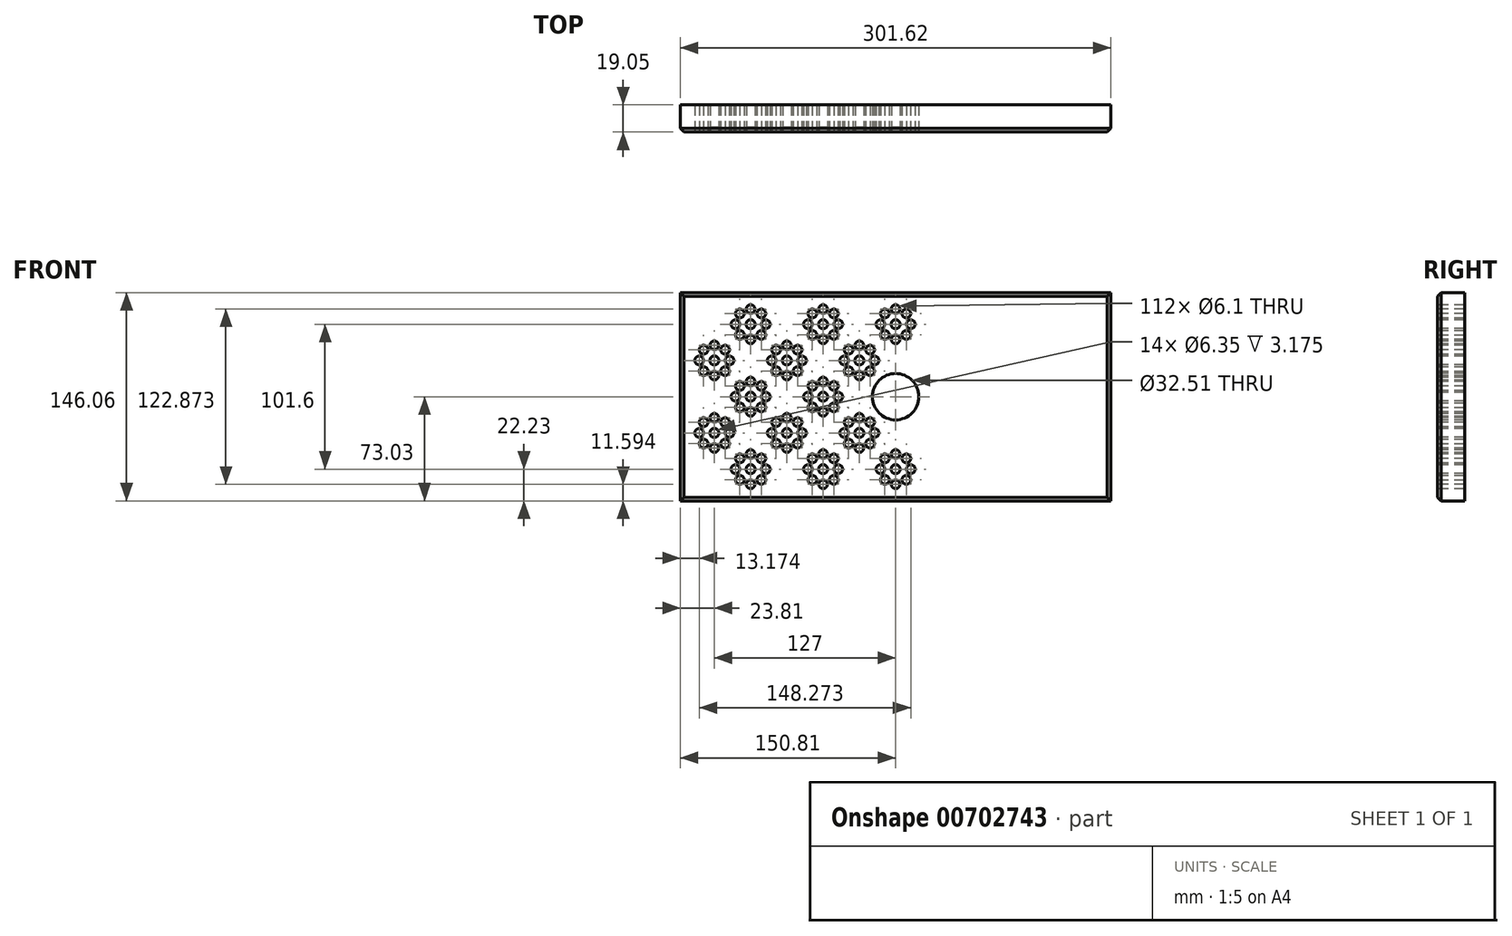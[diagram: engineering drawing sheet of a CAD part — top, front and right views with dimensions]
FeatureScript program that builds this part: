
annotation { "Feature Type Name" : "Feature", "Feature Type Description" : "" }
export const myFeature = defineFeature(function(context is Context, id is Id, definition is map)
    precondition{}
    {
        {
            var Q0;
            Q0=qCreatedBy(makeId("Front.planeOp"),FACE);
            var sketch = newSketch(context, id + "F0", { "sketchPlane" : qUnion([Q0])});
            skLineSegment(sketch, "E0.bottom", {"start": v(-150.81, 73.03) * mm, "end": v(150.81, 73.03) * mm});
            skLineSegment(sketch, "E0.top", {"start": v(-150.81, -73.03) * mm, "end": v(150.81, -73.03) * mm});
            skLineSegment(sketch, "E0.left", {"start": v(-150.81, 73.03) * mm, "end": v(-150.81, -73.03) * mm});
            skLineSegment(sketch, "E0.right", {"start": v(150.81, 73.03) * mm, "end": v(150.81, -73.03) * mm});
            skPoint(sketch, "E0.middle", {"position": v(0, 0) * mm});
            skSolve(sketch);
        }
        {
            var Q0;
            Q0 = qSketchRegion(id + "F0", true);
            extrude(context, id + "F1", {"entities" : qUnion([Q0]), "depth" : 19.05 * mm, "offsetDistance" : 25.4 * mm});
        }
        {
            var Q0;
            Q0=makeQuery(id+"F1.opExtrude","CAP_FACE",FACE,{"disambiguationData":[OSD([sQuery(id+"F0.wireOp",EDGE,"E0.bottom"),sQuery(id+"F0.wireOp",EDGE,"E0.top"),sQuery(id+"F0.wireOp",EDGE,"E0.left"),sQuery(id+"F0.wireOp",EDGE,"E0.right")])],"isStart":false});
            var sketch = newSketch(context, id + "F2", { "sketchPlane" : qUnion([Q0])});
            skLineSegment(sketch, "E1", {"start": v(-150.81, 25.4) * mm, "end": v(150.81, 25.4) * mm, "construction": true});
            skLineSegment(sketch, "E2", {"start": v(-150.81, 0) * mm, "end": v(150.81, 0) * mm, "construction": true});
            skLineSegment(sketch, "E3", {"start": v(-150.81, -25.4) * mm, "end": v(150.81, -25.4) * mm, "construction": true});
            skLineSegment(sketch, "E4", {"start": v(-101.6, 73.03) * mm, "end": v(-101.6, -73.03) * mm, "construction": true});
            skLineSegment(sketch, "E5", {"start": v(-50.8, 73.03) * mm, "end": v(-50.8, -73.03) * mm, "construction": true});
            skCircle(sketch, "E6", {"center": v(0, 0) * mm, "radius": 16.26 * mm});
            skLineSegment(sketch, "E7", {"start": v(-76.2, 73.03) * mm, "end": v(-76.2, -73.03) * mm, "construction": true});
            skLineSegment(sketch, "E8", {"start": v(-25.4, 73.03) * mm, "end": v(-25.4, -73.03) * mm, "construction": true});
            skLineSegment(sketch, "E9", {"start": v(-127, 73.03) * mm, "end": v(-127, -73.03) * mm, "construction": true});
            skCircle(sketch, "E10", {"center": v(-25.4, 25.4) * mm, "radius": 3.18 * mm});
            skCircle(sketch, "E11", {"center": v(-25.4, -25.4) * mm, "radius": 3.18 * mm});
            skCircle(sketch, "E12", {"center": v(-50.8, 0) * mm, "radius": 3.18 * mm});
            skCircle(sketch, "E13", {"center": v(-76.2, 25.4) * mm, "radius": 3.18 * mm});
            skCircle(sketch, "E14", {"center": v(-76.2, -25.4) * mm, "radius": 3.18 * mm});
            skCircle(sketch, "E15", {"center": v(-101.6, 0) * mm, "radius": 3.18 * mm});
            skCircle(sketch, "E16", {"center": v(-127, 25.4) * mm, "radius": 3.18 * mm});
            skCircle(sketch, "E17", {"center": v(-127, -25.4) * mm, "radius": 3.18 * mm});
            skLineSegment(sketch, "E18", {"start": v(-150.81, 50.8) * mm, "end": v(150.81, 50.8) * mm, "construction": true});
            skLineSegment(sketch, "E19", {"start": v(-150.81, -50.8) * mm, "end": v(150.81, -50.8) * mm, "construction": true});
            skCircle(sketch, "E20", {"center": v(-101.6, 50.8) * mm, "radius": 3.18 * mm});
            skCircle(sketch, "E21", {"center": v(-50.8, 50.8) * mm, "radius": 3.18 * mm});
            skCircle(sketch, "E22", {"center": v(0, 50.8) * mm, "radius": 3.18 * mm});
            skCircle(sketch, "E23", {"center": v(0, -50.8) * mm, "radius": 3.18 * mm});
            skCircle(sketch, "E24", {"center": v(-50.8, -50.8) * mm, "radius": 3.18 * mm});
            skCircle(sketch, "E25", {"center": v(-101.6, -50.8) * mm, "radius": 3.18 * mm});
            skSolve(sketch);
        }
        {
            var Q0;
            Q0 = qSketchRegion(id + "F2", true);
            extrude(context, id + "F3", {"entities" : qUnion([Q0]), "operationType" : NewBodyOperationType.REMOVE, "oppositeDirection" : true, "depth" : 3.17 * mm, "offsetDistance" : 25.4 * mm});
        }
        {
            var Q0;
            Q0=makeQuery(id+"F1.opExtrude","CAP_FACE",FACE,{"disambiguationData":[OSD([sQuery(id+"F0.wireOp",EDGE,"E0.bottom"),sQuery(id+"F0.wireOp",EDGE,"E0.top"),sQuery(id+"F0.wireOp",EDGE,"E0.left"),sQuery(id+"F0.wireOp",EDGE,"E0.right")])],"isStart":false});
            var sketch = newSketch(context, id + "F4", { "sketchPlane" : qUnion([Q0])});
            skCircle(sketch, "E26", {"center": v(-127, 25.4) * mm, "radius": 10.64 * mm, "construction": true});
            skCircle(sketch, "E27", {"center": v(-134.52, 32.92) * mm, "radius": 3.05 * mm});
            skCircle(sketch, "E28.1.0", {"center": v(-137.64, 25.4) * mm, "radius": 3.05 * mm});
            skCircle(sketch, "E28.2.0", {"center": v(-134.52, 17.88) * mm, "radius": 3.05 * mm});
            skCircle(sketch, "E29.1.3.0", {"center": v(-127, 14.76) * mm, "radius": 3.05 * mm});
            skCircle(sketch, "E29.1.4.0", {"center": v(-119.48, 17.88) * mm, "radius": 3.05 * mm});
            skCircle(sketch, "E29.1.5.0", {"center": v(-116.36, 25.4) * mm, "radius": 3.05 * mm});
            skCircle(sketch, "E29.1.6.0", {"center": v(-119.48, 32.92) * mm, "radius": 3.05 * mm});
            skCircle(sketch, "E29.1.7.0", {"center": v(-127, 36.04) * mm, "radius": 3.05 * mm});
            skLineSegment(sketch, "E30", {"start": v(-127, 25.4) * mm, "end": v(-127, 36.04) * mm, "construction": true});
            skSolve(sketch);
        }
        {
            var Q0;
            Q0=makeQuery(id+"F4.imprint","IMPRINT",FACE,{"disambiguationData":[TD([[makeQuery(id+"F4.imprint","IMPRINT",EDGE,{"derivedFrom":sQuery(id+"F4.wireOp",EDGE,"E27")}),1.0]])]});
            var Q1;
            Q1=makeQuery(id+"F4.imprint","IMPRINT",FACE,{"disambiguationData":[TD([[makeQuery(id+"F4.imprint","IMPRINT",EDGE,{"derivedFrom":sQuery(id+"F4.wireOp",EDGE,"E28.1.0")}),1.0]])]});
            var Q2;
            Q2=makeQuery(id+"F4.imprint","IMPRINT",FACE,{"disambiguationData":[TD([[makeQuery(id+"F4.imprint","IMPRINT",EDGE,{"derivedFrom":sQuery(id+"F4.wireOp",EDGE,"E28.2.0")}),1.0]])]});
            var Q3;
            Q3=makeQuery(id+"F4.imprint","IMPRINT",FACE,{"disambiguationData":[TD([[makeQuery(id+"F4.imprint","IMPRINT",EDGE,{"derivedFrom":sQuery(id+"F4.wireOp",EDGE,"E29.1.3.0")}),1.0]])]});
            var Q4;
            Q4=makeQuery(id+"F4.imprint","IMPRINT",FACE,{"disambiguationData":[TD([[makeQuery(id+"F4.imprint","IMPRINT",EDGE,{"derivedFrom":sQuery(id+"F4.wireOp",EDGE,"E29.1.4.0")}),1.0]])]});
            var Q5;
            Q5=makeQuery(id+"F4.imprint","IMPRINT",FACE,{"disambiguationData":[TD([[makeQuery(id+"F4.imprint","IMPRINT",EDGE,{"derivedFrom":sQuery(id+"F4.wireOp",EDGE,"E29.1.5.0")}),1.0]])]});
            var Q6;
            Q6=makeQuery(id+"F4.imprint","IMPRINT",FACE,{"disambiguationData":[TD([[makeQuery(id+"F4.imprint","IMPRINT",EDGE,{"derivedFrom":sQuery(id+"F4.wireOp",EDGE,"E29.1.6.0")}),1.0]])]});
            var Q7;
            Q7=makeQuery(id+"F4.imprint","IMPRINT",FACE,{"disambiguationData":[TD([[makeQuery(id+"F4.imprint","IMPRINT",EDGE,{"derivedFrom":sQuery(id+"F4.wireOp",EDGE,"E29.1.7.0")}),1.0]])]});
            extrude(context, id + "F5", {"entities" : qUnion([Q0, Q1, Q2, Q3, Q4, Q5, Q6, Q7]), "operationType" : NewBodyOperationType.REMOVE, "oppositeDirection" : true, "depth" : 25.4 * mm, "offsetDistance" : 25.4 * mm});
        }
        {
            var Q0;
            Q0=makeQuery(id+"F1.opExtrude","CAP_FACE",FACE,{"disambiguationData":[OSD([sQuery(id+"F0.wireOp",EDGE,"E0.bottom"),sQuery(id+"F0.wireOp",EDGE,"E0.top"),sQuery(id+"F0.wireOp",EDGE,"E0.left"),sQuery(id+"F0.wireOp",EDGE,"E0.right")])],"isStart":false});
            var sketch = newSketch(context, id + "F6", { "sketchPlane" : qUnion([Q0])});
            skCircle(sketch, "E31", {"center": v(0, 0) * mm, "radius": 16.26 * mm});
            skSolve(sketch);
        }
        {
            var Q0;
            Q0 = qSketchRegion(id + "F6", true);
            extrude(context, id + "F7", {"entities" : qUnion([Q0]), "operationType" : NewBodyOperationType.REMOVE, "oppositeDirection" : true, "depth" : 25.4 * mm, "offsetDistance" : 25.4 * mm});
        }
        {
            var Q0;
            Q0=makeQuery(id+"F1.opExtrude","CAP_FACE",FACE,{"disambiguationData":[OSD([sQuery(id+"F0.wireOp",EDGE,"E0.bottom"),sQuery(id+"F0.wireOp",EDGE,"E0.top"),sQuery(id+"F0.wireOp",EDGE,"E0.left"),sQuery(id+"F0.wireOp",EDGE,"E0.right")])],"isStart":false});
            var sketch = newSketch(context, id + "F8", { "sketchPlane" : qUnion([Q0])});
            skCircle(sketch, "E32", {"center": v(-76.2, 25.4) * mm, "radius": 10.64 * mm, "construction": true});
            skCircle(sketch, "E33", {"center": v(-83.72, 32.92) * mm, "radius": 3.05 * mm});
            skCircle(sketch, "E34.1.0", {"center": v(-86.84, 25.4) * mm, "radius": 3.05 * mm});
            skCircle(sketch, "E34.2.0", {"center": v(-83.72, 17.88) * mm, "radius": 3.05 * mm});
            skCircle(sketch, "E35.1.3.0", {"center": v(-76.2, 14.76) * mm, "radius": 3.05 * mm});
            skCircle(sketch, "E35.1.4.0", {"center": v(-68.68, 17.88) * mm, "radius": 3.05 * mm});
            skCircle(sketch, "E35.1.5.0", {"center": v(-65.56, 25.4) * mm, "radius": 3.05 * mm});
            skCircle(sketch, "E35.1.6.0", {"center": v(-68.68, 32.92) * mm, "radius": 3.05 * mm});
            skCircle(sketch, "E35.1.7.0", {"center": v(-76.2, 36.04) * mm, "radius": 3.05 * mm});
            skLineSegment(sketch, "E36", {"start": v(-76.2, 25.4) * mm, "end": v(-76.2, 36.04) * mm, "construction": true});
            skCircle(sketch, "E37", {"center": v(-25.4, 25.4) * mm, "radius": 10.64 * mm, "construction": true});
            skCircle(sketch, "E38", {"center": v(-32.92, 32.92) * mm, "radius": 3.05 * mm});
            skCircle(sketch, "E39.1.0", {"center": v(-36.04, 25.4) * mm, "radius": 3.05 * mm});
            skCircle(sketch, "E39.2.0", {"center": v(-32.92, 17.88) * mm, "radius": 3.05 * mm});
            skCircle(sketch, "E40.1.3.0", {"center": v(-25.4, 14.76) * mm, "radius": 3.05 * mm});
            skCircle(sketch, "E40.1.4.0", {"center": v(-17.88, 17.88) * mm, "radius": 3.05 * mm});
            skCircle(sketch, "E40.1.5.0", {"center": v(-14.76, 25.4) * mm, "radius": 3.05 * mm});
            skCircle(sketch, "E40.1.6.0", {"center": v(-17.88, 32.92) * mm, "radius": 3.05 * mm});
            skCircle(sketch, "E40.1.7.0", {"center": v(-25.4, 36.04) * mm, "radius": 3.05 * mm});
            skLineSegment(sketch, "E41", {"start": v(-25.4, 25.4) * mm, "end": v(-25.4, 36.04) * mm, "construction": true});
            skCircle(sketch, "E42", {"center": v(-50.8, 0) * mm, "radius": 10.64 * mm, "construction": true});
            skCircle(sketch, "E43", {"center": v(-58.32, 7.52) * mm, "radius": 3.05 * mm});
            skCircle(sketch, "E44.1.0", {"center": v(-61.44, 0) * mm, "radius": 3.05 * mm});
            skCircle(sketch, "E44.2.0", {"center": v(-58.32, -7.52) * mm, "radius": 3.05 * mm});
            skCircle(sketch, "E45.1.3.0", {"center": v(-50.8, -10.64) * mm, "radius": 3.05 * mm});
            skCircle(sketch, "E45.1.4.0", {"center": v(-43.28, -7.52) * mm, "radius": 3.05 * mm});
            skCircle(sketch, "E45.1.5.0", {"center": v(-40.16, 0) * mm, "radius": 3.05 * mm});
            skCircle(sketch, "E45.1.6.0", {"center": v(-43.28, 7.52) * mm, "radius": 3.05 * mm});
            skCircle(sketch, "E45.1.7.0", {"center": v(-50.8, 10.64) * mm, "radius": 3.05 * mm});
            skLineSegment(sketch, "E46", {"start": v(-50.8, 0) * mm, "end": v(-50.8, 10.64) * mm, "construction": true});
            skCircle(sketch, "E47", {"center": v(-101.6, 0) * mm, "radius": 10.64 * mm, "construction": true});
            skCircle(sketch, "E48", {"center": v(-109.12, 7.52) * mm, "radius": 3.05 * mm});
            skCircle(sketch, "E49.1.0", {"center": v(-112.24, 0) * mm, "radius": 3.05 * mm});
            skCircle(sketch, "E49.2.0", {"center": v(-109.12, -7.52) * mm, "radius": 3.05 * mm});
            skCircle(sketch, "E50.1.3.0", {"center": v(-101.6, -10.64) * mm, "radius": 3.05 * mm});
            skCircle(sketch, "E50.1.4.0", {"center": v(-94.08, -7.52) * mm, "radius": 3.05 * mm});
            skCircle(sketch, "E50.1.5.0", {"center": v(-90.96, 0) * mm, "radius": 3.05 * mm});
            skCircle(sketch, "E50.1.6.0", {"center": v(-94.08, 7.52) * mm, "radius": 3.05 * mm});
            skCircle(sketch, "E50.1.7.0", {"center": v(-101.6, 10.64) * mm, "radius": 3.05 * mm});
            skLineSegment(sketch, "E51", {"start": v(-101.6, 0) * mm, "end": v(-101.6, 10.64) * mm, "construction": true});
            skCircle(sketch, "E52", {"center": v(-127, -25.4) * mm, "radius": 10.64 * mm, "construction": true});
            skCircle(sketch, "E53", {"center": v(-119.48, -32.92) * mm, "radius": 3.05 * mm});
            skCircle(sketch, "E54.1.0", {"center": v(-116.36, -25.4) * mm, "radius": 3.05 * mm});
            skCircle(sketch, "E54.2.0", {"center": v(-119.48, -17.88) * mm, "radius": 3.05 * mm});
            skCircle(sketch, "E55.1.3.0", {"center": v(-127, -14.76) * mm, "radius": 3.05 * mm});
            skCircle(sketch, "E55.1.4.0", {"center": v(-134.52, -17.88) * mm, "radius": 3.05 * mm});
            skCircle(sketch, "E55.1.5.0", {"center": v(-137.64, -25.4) * mm, "radius": 3.05 * mm});
            skCircle(sketch, "E55.1.6.0", {"center": v(-134.52, -32.92) * mm, "radius": 3.05 * mm});
            skCircle(sketch, "E55.1.7.0", {"center": v(-127, -36.04) * mm, "radius": 3.05 * mm});
            skLineSegment(sketch, "E56", {"start": v(-127, -36.04) * mm, "end": v(-127, -25.4) * mm, "construction": true});
            skCircle(sketch, "E57", {"center": v(-76.2, -25.4) * mm, "radius": 10.64 * mm, "construction": true});
            skCircle(sketch, "E58", {"center": v(-68.68, -32.92) * mm, "radius": 3.05 * mm});
            skCircle(sketch, "E59.1.0", {"center": v(-65.56, -25.4) * mm, "radius": 3.05 * mm});
            skCircle(sketch, "E59.2.0", {"center": v(-68.68, -17.88) * mm, "radius": 3.05 * mm});
            skCircle(sketch, "E60.1.3.0", {"center": v(-76.2, -14.76) * mm, "radius": 3.05 * mm});
            skCircle(sketch, "E60.1.4.0", {"center": v(-83.72, -17.88) * mm, "radius": 3.05 * mm});
            skCircle(sketch, "E60.1.5.0", {"center": v(-86.84, -25.4) * mm, "radius": 3.05 * mm});
            skCircle(sketch, "E60.1.6.0", {"center": v(-83.72, -32.92) * mm, "radius": 3.05 * mm});
            skCircle(sketch, "E60.1.7.0", {"center": v(-76.2, -36.04) * mm, "radius": 3.05 * mm});
            skLineSegment(sketch, "E61", {"start": v(-76.2, -36.04) * mm, "end": v(-76.2, -25.4) * mm, "construction": true});
            skCircle(sketch, "E62", {"center": v(-25.4, -25.4) * mm, "radius": 10.64 * mm, "construction": true});
            skCircle(sketch, "E63", {"center": v(-17.88, -32.92) * mm, "radius": 3.05 * mm});
            skCircle(sketch, "E64.1.0", {"center": v(-14.76, -25.4) * mm, "radius": 3.05 * mm});
            skCircle(sketch, "E64.2.0", {"center": v(-17.88, -17.88) * mm, "radius": 3.05 * mm});
            skCircle(sketch, "E65.1.3.0", {"center": v(-25.4, -14.76) * mm, "radius": 3.05 * mm});
            skCircle(sketch, "E65.1.4.0", {"center": v(-32.92, -17.88) * mm, "radius": 3.05 * mm});
            skCircle(sketch, "E65.1.5.0", {"center": v(-36.04, -25.4) * mm, "radius": 3.05 * mm});
            skCircle(sketch, "E65.1.6.0", {"center": v(-32.92, -32.92) * mm, "radius": 3.05 * mm});
            skCircle(sketch, "E65.1.7.0", {"center": v(-25.4, -36.04) * mm, "radius": 3.05 * mm});
            skLineSegment(sketch, "E66", {"start": v(-25.4, -36.04) * mm, "end": v(-25.4, -25.4) * mm, "construction": true});
            skCircle(sketch, "E67", {"center": v(-101.6, 50.8) * mm, "radius": 10.64 * mm, "construction": true});
            skCircle(sketch, "E68", {"center": v(-109.12, 58.32) * mm, "radius": 3.05 * mm});
            skCircle(sketch, "E69.1.0", {"center": v(-112.24, 50.8) * mm, "radius": 3.05 * mm});
            skCircle(sketch, "E69.2.0", {"center": v(-109.12, 43.28) * mm, "radius": 3.05 * mm});
            skCircle(sketch, "E70.1.3.0", {"center": v(-101.6, 40.16) * mm, "radius": 3.05 * mm});
            skCircle(sketch, "E70.1.4.0", {"center": v(-94.08, 43.28) * mm, "radius": 3.05 * mm});
            skCircle(sketch, "E70.1.5.0", {"center": v(-90.96, 50.8) * mm, "radius": 3.05 * mm});
            skCircle(sketch, "E70.1.6.0", {"center": v(-94.08, 58.32) * mm, "radius": 3.05 * mm});
            skCircle(sketch, "E70.1.7.0", {"center": v(-101.6, 61.44) * mm, "radius": 3.05 * mm});
            skLineSegment(sketch, "E71", {"start": v(-101.6, 50.8) * mm, "end": v(-101.6, 61.44) * mm, "construction": true});
            skCircle(sketch, "E72", {"center": v(-50.8, 50.8) * mm, "radius": 10.64 * mm, "construction": true});
            skCircle(sketch, "E73", {"center": v(-58.32, 58.32) * mm, "radius": 3.05 * mm});
            skCircle(sketch, "E74.1.0", {"center": v(-61.44, 50.8) * mm, "radius": 3.05 * mm});
            skCircle(sketch, "E74.2.0", {"center": v(-58.32, 43.28) * mm, "radius": 3.05 * mm});
            skCircle(sketch, "E75.1.3.0", {"center": v(-50.8, 40.16) * mm, "radius": 3.05 * mm});
            skCircle(sketch, "E75.1.4.0", {"center": v(-43.28, 43.28) * mm, "radius": 3.05 * mm});
            skCircle(sketch, "E75.1.5.0", {"center": v(-40.16, 50.8) * mm, "radius": 3.05 * mm});
            skCircle(sketch, "E75.1.6.0", {"center": v(-43.28, 58.32) * mm, "radius": 3.05 * mm});
            skCircle(sketch, "E75.1.7.0", {"center": v(-50.8, 61.44) * mm, "radius": 3.05 * mm});
            skLineSegment(sketch, "E76", {"start": v(-50.8, 50.8) * mm, "end": v(-50.8, 61.44) * mm, "construction": true});
            skCircle(sketch, "E77", {"center": v(0, 50.8) * mm, "radius": 10.64 * mm, "construction": true});
            skCircle(sketch, "E78", {"center": v(-7.52, 58.32) * mm, "radius": 3.05 * mm});
            skCircle(sketch, "E79.1.0", {"center": v(-10.64, 50.8) * mm, "radius": 3.05 * mm});
            skCircle(sketch, "E79.2.0", {"center": v(-7.52, 43.28) * mm, "radius": 3.05 * mm});
            skCircle(sketch, "E80.1.3.0", {"center": v(0, 40.16) * mm, "radius": 3.05 * mm});
            skCircle(sketch, "E80.1.4.0", {"center": v(7.52, 43.28) * mm, "radius": 3.05 * mm});
            skCircle(sketch, "E80.1.5.0", {"center": v(10.64, 50.8) * mm, "radius": 3.05 * mm});
            skCircle(sketch, "E80.1.6.0", {"center": v(7.52, 58.32) * mm, "radius": 3.05 * mm});
            skCircle(sketch, "E80.1.7.0", {"center": v(0, 61.44) * mm, "radius": 3.05 * mm});
            skLineSegment(sketch, "E81", {"start": v(0, 50.8) * mm, "end": v(0, 61.44) * mm, "construction": true});
            skCircle(sketch, "E82", {"center": v(-101.6, -50.8) * mm, "radius": 10.64 * mm, "construction": true});
            skCircle(sketch, "E83", {"center": v(-109.12, -43.28) * mm, "radius": 3.05 * mm});
            skCircle(sketch, "E84.1.0", {"center": v(-112.24, -50.8) * mm, "radius": 3.05 * mm});
            skCircle(sketch, "E84.2.0", {"center": v(-109.12, -58.32) * mm, "radius": 3.05 * mm});
            skCircle(sketch, "E85.1.3.0", {"center": v(-101.6, -61.44) * mm, "radius": 3.05 * mm});
            skCircle(sketch, "E85.1.4.0", {"center": v(-94.08, -58.32) * mm, "radius": 3.05 * mm});
            skCircle(sketch, "E85.1.5.0", {"center": v(-90.96, -50.8) * mm, "radius": 3.05 * mm});
            skCircle(sketch, "E85.1.6.0", {"center": v(-94.08, -43.28) * mm, "radius": 3.05 * mm});
            skCircle(sketch, "E85.1.7.0", {"center": v(-101.6, -40.16) * mm, "radius": 3.05 * mm});
            skLineSegment(sketch, "E86", {"start": v(-101.6, -50.8) * mm, "end": v(-101.6, -40.16) * mm, "construction": true});
            skCircle(sketch, "E87", {"center": v(-50.8, -50.8) * mm, "radius": 10.64 * mm, "construction": true});
            skCircle(sketch, "E88", {"center": v(-58.32, -43.28) * mm, "radius": 3.05 * mm});
            skCircle(sketch, "E89.1.0", {"center": v(-61.44, -50.8) * mm, "radius": 3.05 * mm});
            skCircle(sketch, "E89.2.0", {"center": v(-58.32, -58.32) * mm, "radius": 3.05 * mm});
            skCircle(sketch, "E90.1.3.0", {"center": v(-50.8, -61.44) * mm, "radius": 3.05 * mm});
            skCircle(sketch, "E90.1.4.0", {"center": v(-43.28, -58.32) * mm, "radius": 3.05 * mm});
            skCircle(sketch, "E90.1.5.0", {"center": v(-40.16, -50.8) * mm, "radius": 3.05 * mm});
            skCircle(sketch, "E90.1.6.0", {"center": v(-43.28, -43.28) * mm, "radius": 3.05 * mm});
            skCircle(sketch, "E90.1.7.0", {"center": v(-50.8, -40.16) * mm, "radius": 3.05 * mm});
            skLineSegment(sketch, "E91", {"start": v(-50.8, -50.8) * mm, "end": v(-50.8, -40.16) * mm, "construction": true});
            skCircle(sketch, "E92", {"center": v(0, -50.8) * mm, "radius": 10.64 * mm, "construction": true});
            skCircle(sketch, "E93", {"center": v(-7.52, -43.28) * mm, "radius": 3.05 * mm});
            skCircle(sketch, "E94.1.0", {"center": v(-10.64, -50.8) * mm, "radius": 3.05 * mm});
            skCircle(sketch, "E94.2.0", {"center": v(-7.52, -58.32) * mm, "radius": 3.05 * mm});
            skCircle(sketch, "E95.1.3.0", {"center": v(0, -61.44) * mm, "radius": 3.05 * mm});
            skCircle(sketch, "E95.1.4.0", {"center": v(7.52, -58.32) * mm, "radius": 3.05 * mm});
            skCircle(sketch, "E95.1.5.0", {"center": v(10.64, -50.8) * mm, "radius": 3.05 * mm});
            skCircle(sketch, "E95.1.6.0", {"center": v(7.52, -43.28) * mm, "radius": 3.05 * mm});
            skCircle(sketch, "E95.1.7.0", {"center": v(0, -40.16) * mm, "radius": 3.05 * mm});
            skLineSegment(sketch, "E96", {"start": v(0, -50.8) * mm, "end": v(0, -40.16) * mm, "construction": true});
            skSolve(sketch);
        }
        {
            var Q0;
            Q0 = qSketchRegion(id + "F8", true);
            extrude(context, id + "F9", {"entities" : qUnion([Q0]), "operationType" : NewBodyOperationType.REMOVE, "oppositeDirection" : true, "depth" : 25.4 * mm, "offsetDistance" : 25.4 * mm});
        }
        {
            var Q0;
            Q0=makeQuery(id+"F3.boolean.opBoolean","COPY",EDGE,{"derivedFrom":makeQuery(id+"F3.opExtrude","CAP_EDGE",EDGE,{"disambiguationData":[OSD([sQuery(id+"F2.wireOp",EDGE,"E6")])],"isStart":true})});
            var Q1;
            Q1=makeQuery(id+"F1.opExtrude","CAP_EDGE",EDGE,{"disambiguationData":[OSD([sQuery(id+"F0.wireOp",EDGE,"E0.bottom")])],"isStart":false});
            var Q2;
            Q2=makeQuery(id+"F1.opExtrude","CAP_EDGE",EDGE,{"disambiguationData":[OSD([sQuery(id+"F0.wireOp",EDGE,"E0.right")])],"isStart":false});
            var Q3;
            Q3=makeQuery(id+"F1.opExtrude","CAP_EDGE",EDGE,{"disambiguationData":[OSD([sQuery(id+"F0.wireOp",EDGE,"E0.top")])],"isStart":false});
            var Q4;
            Q4=makeQuery(id+"F1.opExtrude","CAP_EDGE",EDGE,{"disambiguationData":[OSD([sQuery(id+"F0.wireOp",EDGE,"E0.left")])],"isStart":false});
            chamfer(context, id + "F10", {"entities" : qUnion([Q0, Q1, Q2, Q3, Q4]), "width" : 2.54 * mm, "tangentPropagation" : true});
        }
    });
